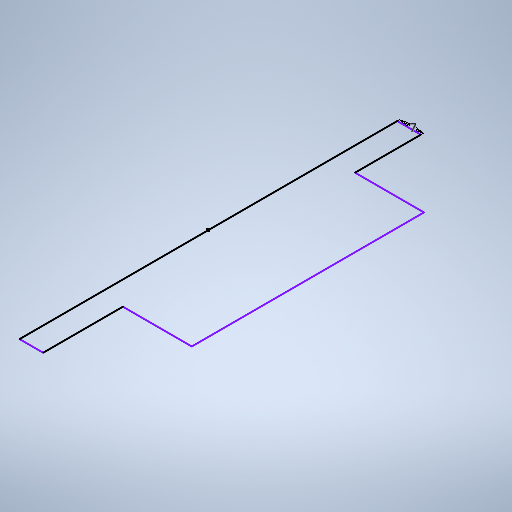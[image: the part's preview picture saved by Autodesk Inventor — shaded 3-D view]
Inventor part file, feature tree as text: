
AUTODESK INVENTOR PART (.ipt)
format: ipt  version: 2025.1 (Build 291241000, 241)  size: 251,392 bytes
history: native  units: mm
features: sketch x1
ambient origin geometry x8: Origin, YZ Plane, XZ Plane, XY Plane, X Axis, Y Axis, Z Axis, Center Point
feature tree (1):
  sketch  "Sketch1"  dims[d0=7.0mm]
